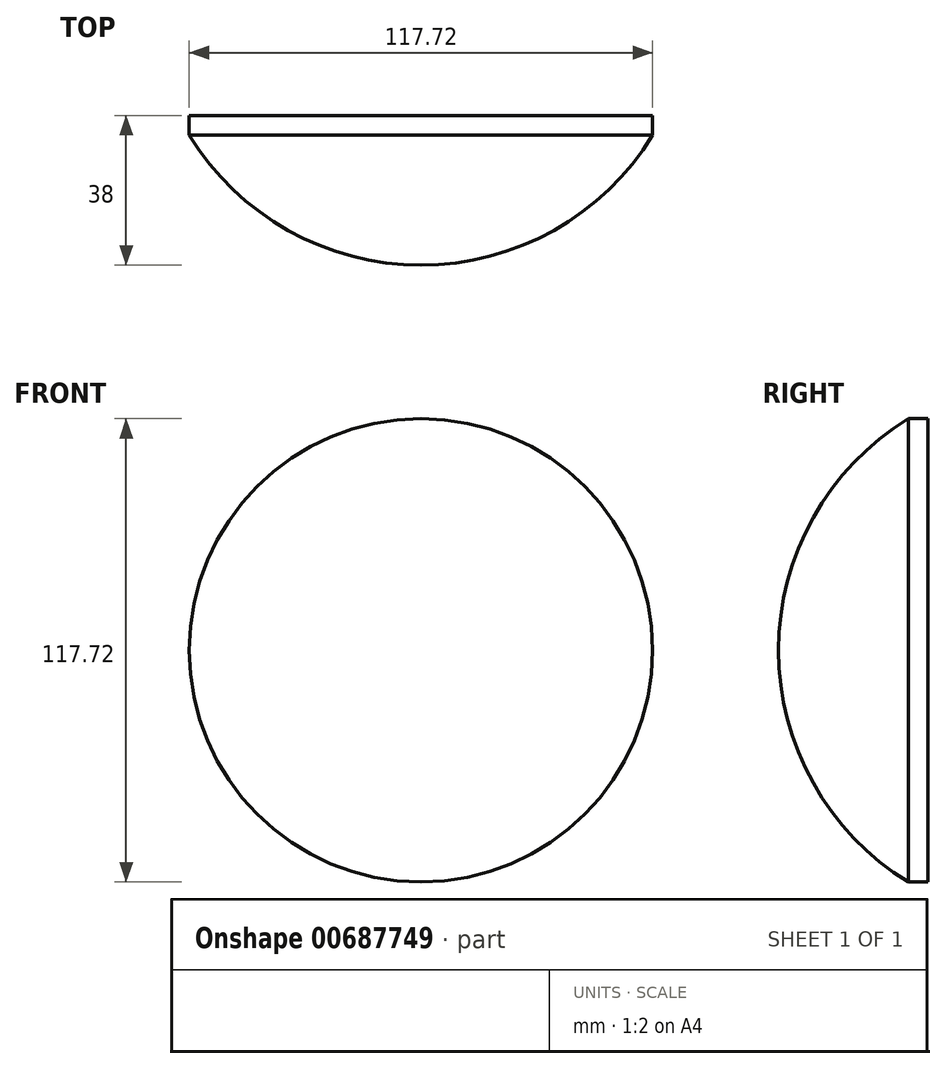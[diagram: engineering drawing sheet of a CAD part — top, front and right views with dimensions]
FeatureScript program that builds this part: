
annotation { "Feature Type Name" : "Feature", "Feature Type Description" : "" }
export const myFeature = defineFeature(function(context is Context, id is Id, definition is map)
    precondition{}
    {
        {
            var Q0;
            Q0=qCreatedBy(makeId("Front.planeOp"),FACE);
            var sketch = newSketch(context, id + "F0", { "sketchPlane" : qUnion([Q0])});
            skArc(sketch, "E0", {"start": v(0, -69) * mm, "mid": v(69, 0) * mm, "end": v(0, 69) * mm});
            skLineSegment(sketch, "E1", {"start": v(0, 69) * mm, "end": v(0, -69) * mm});
            skSolve(sketch);
        }
        {
            var Q0;
            Q0 = qSketchRegion(id + "F0", true);
            var Q1;
            Q1=sQuery(id+"F0.wireOp",EDGE,"E1");
            revolve(context, id + "F1", {"entities" : qUnion([Q0]), "axis" : qUnion([Q1]), "revolveType" : RevolveType.ONE_DIRECTION, "angle" : 180 * degree});
        }
        {
            var Q0;
            Q0=makeQuery(id+"F1.opRevolve","CAP_FACE",FACE,{"disambiguationData":[OSD([sQuery(id+"F0.wireOp",EDGE,"E0"),sQuery(id+"F0.wireOp",EDGE,"E1")])],"isStart":true});
            var sketch = newSketch(context, id + "F2", { "sketchPlane" : qUnion([Q0])});
            skCircle(sketch, "E2.0.0", {"center": v(0, 0) * mm, "radius": 69 * mm});
            skSolve(sketch);
        }
        {
            var Q0;
            Q0 = qSketchRegion(id + "F2", true);
            extrude(context, id + "F3", {"entities" : qUnion([Q0]), "operationType" : NewBodyOperationType.REMOVE, "oppositeDirection" : true, "depth" : 36 * mm, "offsetDistance" : 25 * mm});
        }
        {
            var Q0;
            Q0=makeQuery(id+"F3.boolean.opBoolean","COPY",FACE,{"derivedFrom":makeQuery(id+"F3.opExtrude","CAP_FACE",FACE,{"disambiguationData":[OSD([sQuery(id+"F2.wireOp",EDGE,"E2.0.0")])],"isStart":false})});
            var sketch = newSketch(context, id + "F4", { "sketchPlane" : qUnion([Q0])});
            skCircle(sketch, "E3.0.0", {"center": v(0, 0) * mm, "radius": 58.86 * mm});
            skSolve(sketch);
        }
        {
            var Q0;
            Q0 = qSketchRegion(id + "F4", true);
            extrude(context, id + "F5", {"entities" : qUnion([Q0]), "operationType" : NewBodyOperationType.ADD, "depth" : 5 * mm, "offsetDistance" : 25 * mm});
        }
    });
